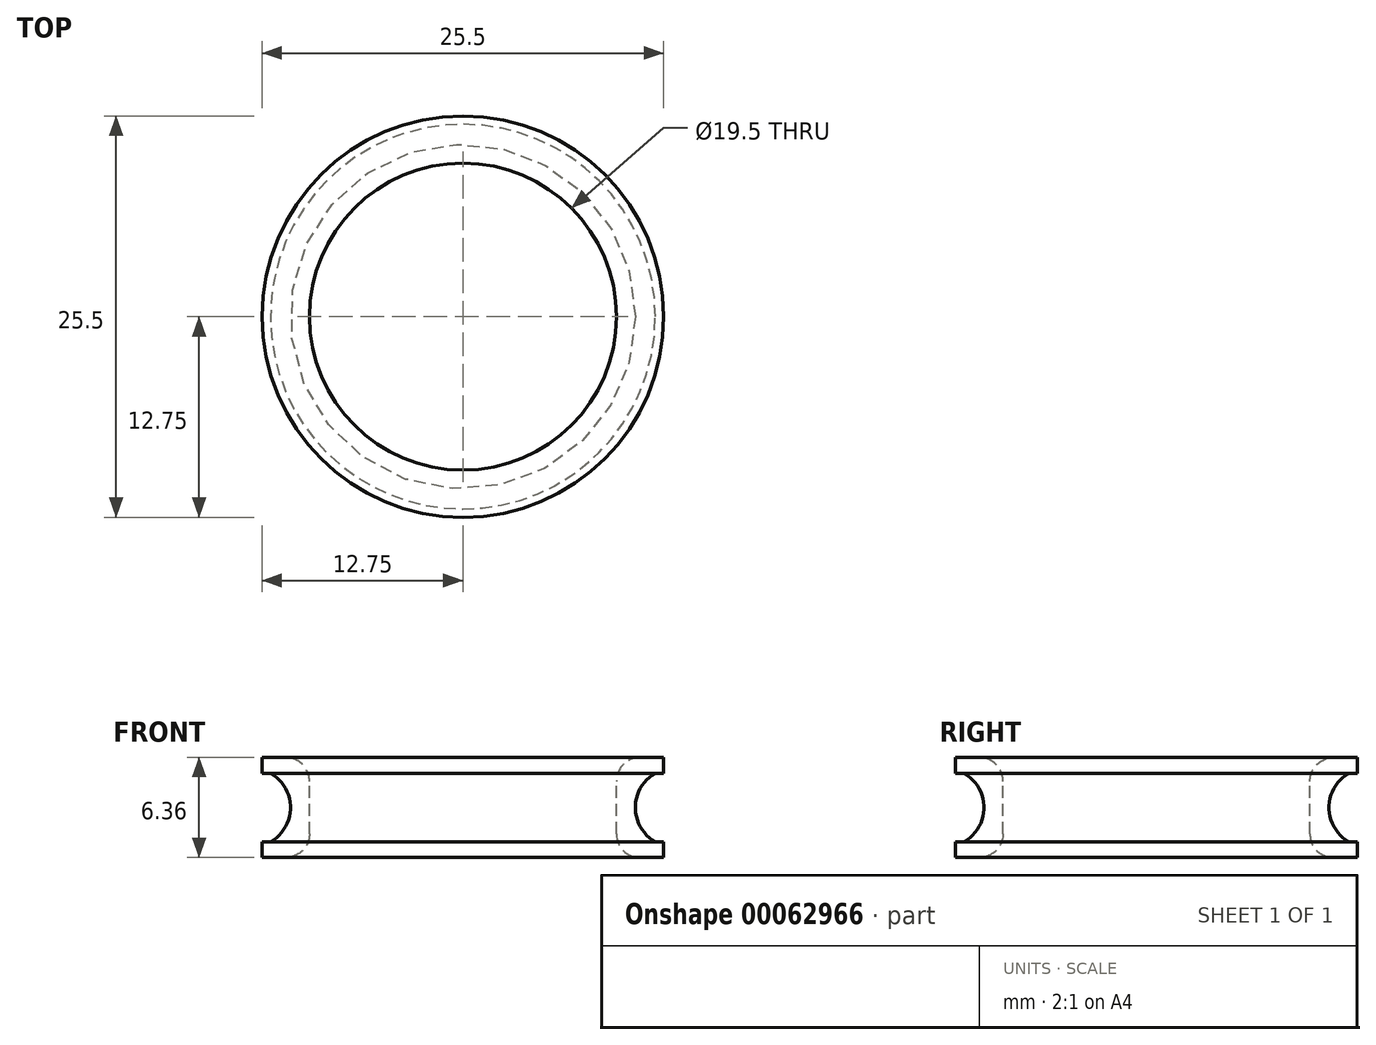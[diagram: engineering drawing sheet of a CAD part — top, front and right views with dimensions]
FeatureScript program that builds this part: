
annotation { "Feature Type Name" : "Feature", "Feature Type Description" : "" }
export const myFeature = defineFeature(function(context is Context, id is Id, definition is map)
    precondition{}
    {
        {
            var Q0;
            Q0=qCreatedBy(makeId("Front.planeOp"),FACE);
            var sketch = newSketch(context, id + "F0", { "sketchPlane" : qUnion([Q0])});
            skLineSegment(sketch, "E0", {"start": v(-9.75, 1.67) * mm, "end": v(-9.75, -1.68) * mm});
            skLineSegment(sketch, "E1", {"start": v(-11.25, 3.17) * mm, "end": v(-12.75, 3.17) * mm});
            skLineSegment(sketch, "E2", {"start": v(-12.75, 3.17) * mm, "end": v(-12.75, 2.17) * mm});
            skLineSegment(sketch, "E3", {"start": v(-12.75, 2.17) * mm, "end": v(-12.22, 2.17) * mm});
            skArc(sketch, "E4", {"start": v(-10.95, 0) * mm, "mid": v(-11.29, 1.26) * mm, "end": v(-12.22, 2.18) * mm});
            skLineSegment(sketch, "E5", {"start": v(0, 0) * mm, "end": v(-10.95, 0) * mm, "construction": true});
            skLineSegment(sketch, "E6.MirrorCS", {"start": v(-11.25, -3.18) * mm, "end": v(-12.75, -3.18) * mm});
            skLineSegment(sketch, "E7.MirrorCS", {"start": v(-12.75, -3.18) * mm, "end": v(-12.75, -2.18) * mm});
            skLineSegment(sketch, "E8.MirrorCS", {"start": v(-12.75, -2.18) * mm, "end": v(-12.22, -2.18) * mm});
            skArc(sketch, "E9.MirrorCS", {"start": v(-10.95, 0) * mm, "mid": v(-11.29, -1.26) * mm, "end": v(-12.22, -2.18) * mm});
            skLineSegment(sketch, "E10", {"start": v(0, 3.17) * mm, "end": v(0, -2.23) * mm, "construction": true});
            skArc(sketch, "E11", {"start": v(-9.75, 1.67) * mm, "mid": v(-10.19, 2.74) * mm, "end": v(-11.25, 3.17) * mm});
            skArc(sketch, "E12.MirrorCS", {"start": v(-9.75, -1.68) * mm, "mid": v(-10.19, -2.74) * mm, "end": v(-11.25, -3.18) * mm});
            skPoint(sketch, "E13.orphan", {"position": v(-9.75, 3.17) * mm});
            skPoint(sketch, "E14.orphan", {"position": v(-9.75, -3.18) * mm});
            skSolve(sketch);
        }
        {
            var Q0;
            Q0=makeQuery(id+"F0.imprint","IMPRINT",FACE,{"disambiguationData":[TD([[makeQuery(id+"F0.imprint","IMPRINT",EDGE,{"derivedFrom":sQuery(id+"F0.wireOp",EDGE,"E0")}),-1.0]])]});
            var Q1;
            Q1=sQuery(id+"F0.wireOp",EDGE,"E10");
            revolve(context, id + "F1", {"entities" : qUnion([Q0]), "axis" : qUnion([Q1]), "revolveType" : RevolveType.FULL});
        }
    });
